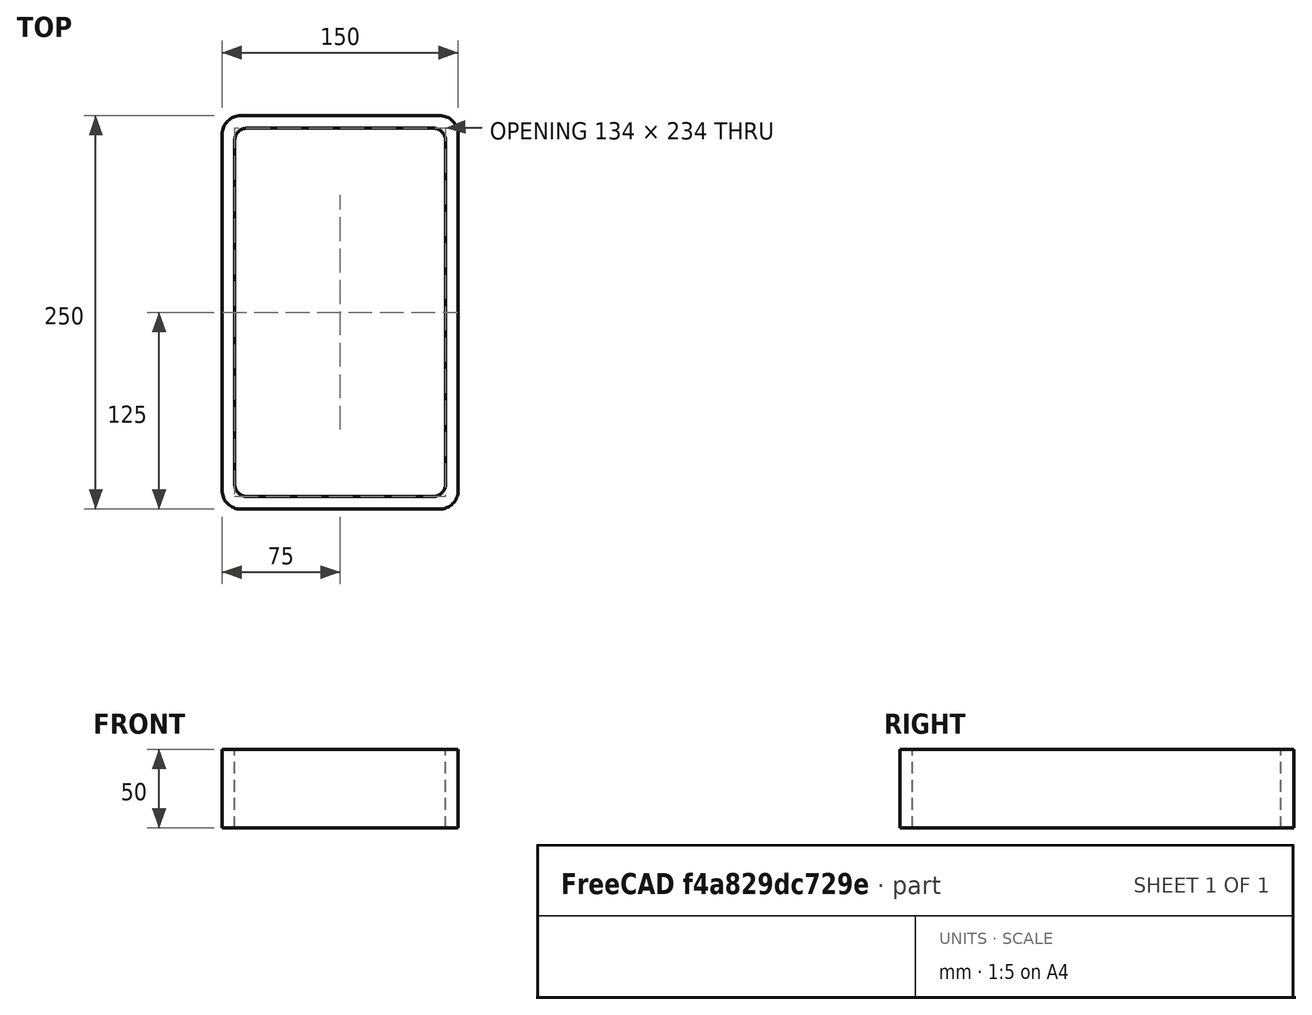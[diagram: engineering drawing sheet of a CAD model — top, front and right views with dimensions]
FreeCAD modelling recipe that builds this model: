
FCSTD DOCUMENT  (FreeCAD 0.15R4671 (Git))
Label: Rectangular hollow section 250x150x8 EN10219 S235JRH
License: All rights reserved
LicenseURL: http://en.wikipedia.org/wiki/All_rights_reserved
objects: Sketcher::SketchObject×1, Part::Extrusion×1
note: 2 computed .brp shape members not serialized (recipe doc carries the construction recipe); baked Part::Feature solids carry a one-line shape summary decoded from their .brp

FEATURE [Sketcher::SketchObject] Sketch
  sketch-geometry (16):
    g0: LineSegment StartX=-59 StartY=117 StartZ=0 EndX=59 EndY=117 EndZ=0
    g1: LineSegment StartX=67 StartY=109 StartZ=0 EndX=67 EndY=-109 EndZ=0
    g2: LineSegment StartX=59 StartY=-117 StartZ=0 EndX=-59 EndY=-117 EndZ=0
    g3: LineSegment StartX=-67 StartY=-109 StartZ=0 EndX=-67 EndY=109 EndZ=0
    g4: LineSegment StartX=-63 StartY=125 StartZ=0 EndX=63 EndY=125 EndZ=0
    g5: LineSegment StartX=75 StartY=113 StartZ=0 EndX=75 EndY=-113 EndZ=0
    g6: LineSegment StartX=63 StartY=-125 StartZ=0 EndX=-63 EndY=-125 EndZ=0
    g7: LineSegment StartX=-75 StartY=-113 StartZ=0 EndX=-75 EndY=113 EndZ=0
    g8: ArcOfCircle CenterX=-59 CenterY=109 CenterZ=0 NormalX=0 NormalY=0 NormalZ=1 Radius=8 StartAngle=1.5708 EndAngle=3.14159
    g9: ArcOfCircle CenterX=59 CenterY=109 CenterZ=0 NormalX=0 NormalY=0 NormalZ=1 Radius=8 StartAngle=0 EndAngle=1.5708
    g10: ArcOfCircle CenterX=59 CenterY=-109 CenterZ=0 NormalX=0 NormalY=0 NormalZ=1 Radius=8 StartAngle=4.71239 EndAngle=6.28319
    g11: ArcOfCircle CenterX=-59 CenterY=-109 CenterZ=0 NormalX=0 NormalY=0 NormalZ=1 Radius=8 StartAngle=3.14159 EndAngle=4.71239
    g12: ArcOfCircle CenterX=63 CenterY=113 CenterZ=0 NormalX=0 NormalY=0 NormalZ=1 Radius=12 StartAngle=0 EndAngle=1.5708
    g13: ArcOfCircle CenterX=63 CenterY=-113 CenterZ=0 NormalX=0 NormalY=0 NormalZ=1 Radius=12 StartAngle=4.71239 EndAngle=6.28319
    g14: ArcOfCircle CenterX=-63 CenterY=-113 CenterZ=0 NormalX=0 NormalY=0 NormalZ=1 Radius=12 StartAngle=3.14159 EndAngle=4.71239
    g15: ArcOfCircle CenterX=-63 CenterY=113 CenterZ=0 NormalX=0 NormalY=0 NormalZ=1 Radius=12 StartAngle=1.5708 EndAngle=3.14159
  constraints (36):
    c: Horizontal(g2)
    c: Vertical(g3)
    c: Horizontal(g6)
    c: Vertical(g7)
    c: Tangent(g3,g8) = 1.5708
    c: Tangent(g0,g8) = 1.5708
    c: Tangent(g0,g9) = 1.5708
    c: Tangent(g1,g9) = 1.5708
    c: Tangent(g1,g10) = 1.5708
    c: Tangent(g2,g10) = 1.5708
    c: Tangent(g2,g11) = 1.5708
    c: Tangent(g3,g11) = 1.5708
    c: Tangent(g4,g12) = 1.5708
    c: Tangent(g5,g12) = 1.5708
    c: Tangent(g5,g13) = 1.5708
    c: Tangent(g6,g13) = 1.5708
    c: Tangent(g6,g14) = 1.5708
    c: Tangent(g7,g14) = 1.5708
    c: Tangent(g7,g15) = 1.5708
    c: Tangent(g4,g15) = 1.5708
    c: Equal(g9,g8)
    c: Equal(g9,g11)
    c: Equal(g9,g10)
    c: Equal(g12,g15)
    c: Equal(g12,g14)
    c: Equal(g12,g13)
    c: Symmetric(g4,g6,g-1)
    c: Symmetric(g7,g5,g-2)
    c: DistanceY(g4,g6) = -250
    c: DistanceX(g7,g5) = 150
    c: Symmetric(g3,g1,g-2)
    c: Symmetric(g0,g2,g-1)
    c: DistanceY(g0,g4) = 8
    c: DistanceX(g5,g1) = -8
    c: Radius(g9) = 8
    c: Radius(g12) = 12
FEATURE [Part::Extrusion] Extrude  label="Rectangular hollow section 250x150x8 EN10219 S235JRH"
  Base = -> Sketch
  Dir = (0,0,50)
  Solid = true
